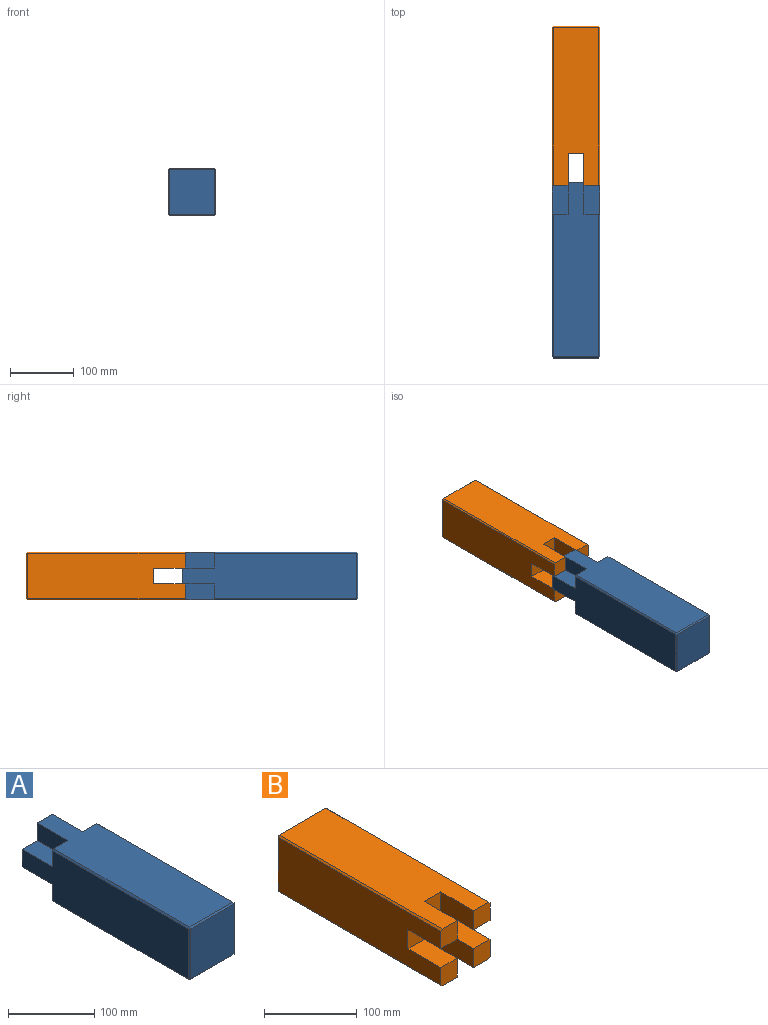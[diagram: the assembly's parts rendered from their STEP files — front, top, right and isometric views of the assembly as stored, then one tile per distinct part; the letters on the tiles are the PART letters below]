
ASSEMBLY  parts=2 mates=1
PART A: 30 faces, bbox 75x275x75 mm
  f0: plane 273x71mm, normal (1,0,0), area 17083mm2, adj f2,f10,f11,f12,f14,f18,f19,f20
  f1: plane 273x71mm, normal (0,0,-1), area 17083mm2, adj f2,f13,f14,f16,f17,f20,f25,f26
  f2: plane 75x75mm, normal (0,1,0), area 3125mm2, adj f0,f1,f3,f4,f6,f7,f9,f10
  f3: plane 273x71mm, normal (0,0,1), area 17083mm2, adj f2,f7,f8,f9,f11,f18,f23,f24
  f4: plane 273x71mm, normal (-1,0,0), area 17083mm2, adj f2,f6,f8,f15,f17,f23,f26,f29
  f5: plane 71x71mm, normal (0,-1,0), area 5041mm2, adj f19,f24,f25,f29
  f6: plane 50x25mm, normal (0,0,1), area 1250mm2, adj f2,f4,f7,f8
  f7: plane 50x25mm, normal (-1,0,0), area 1250mm2, adj f2,f3,f6,f8
  f8: plane 25x25mm, normal (0,1,0), area 623mm2, adj f3,f4,f6,f7,f23
  f9: plane 50x25mm, normal (1,0,0), area 1250mm2, adj f2,f3,f10,f11
  f10: plane 50x25mm, normal (0,0,1), area 1250mm2, adj f0,f2,f9,f11
  f11: plane 25x25mm, normal (0,1,0), area 623mm2, adj f0,f3,f9,f10,f18
  f12: plane 50x25mm, normal (0,0,-1), area 1250mm2, adj f0,f2,f13,f14
  f13: plane 50x25mm, normal (1,0,0), area 1250mm2, adj f1,f2,f12,f14
  f14: plane 25x25mm, normal (0,1,0), area 623mm2, adj f0,f1,f12,f13,f20
  f15: plane 50x25mm, normal (0,0,-1), area 1250mm2, adj f2,f4,f16,f17
  f16: plane 50x25mm, normal (-1,0,0), area 1250mm2, adj f1,f2,f15,f17
  f17: plane 25x25mm, normal (0,1,0), area 623mm2, adj f1,f4,f15,f16,f26
  f18: plane 223x2mm, normal (0.71,0,0.71), area 630.7mm2, adj f0,f3,f11,f21
  f19: plane 71x2mm, normal (0.71,-0.71,0), area 200.8mm2, adj f0,f5,f21,f22
  f20: plane 223x2mm, normal (0.71,0,-0.71), area 630.7mm2, adj f0,f1,f14,f22
  f21: plane 2x2mm, normal (0.58,-0.58,0.58), area 3.5mm2, adj f18,f19,f24
  f22: plane 2x2mm, normal (0.58,-0.58,-0.58), area 3.5mm2, adj f19,f20,f25
  f23: plane 223x2mm, normal (-0.71,0,0.71), area 630.7mm2, adj f3,f4,f8,f27
  f24: plane 71x2mm, normal (0,-0.71,0.71), area 200.8mm2, adj f3,f5,f21,f27
  f25: plane 71x2mm, normal (0,-0.71,-0.71), area 200.8mm2, adj f1,f5,f22,f28
  f26: plane 223x2mm, normal (-0.71,0,-0.71), area 630.7mm2, adj f1,f4,f17,f28
  f27: plane 2x2mm, normal (-0.58,-0.58,0.58), area 3.5mm2, adj f23,f24,f29
  f28: plane 2x2mm, normal (-0.58,-0.58,-0.58), area 3.5mm2, adj f25,f26,f29
  f29: plane 71x2mm, normal (-0.71,-0.71,0), area 200.8mm2, adj f4,f5,f27,f28
PART B: 30 faces, bbox 75x250x75 mm
  f0: plane 75x75mm, normal (0,-1,0), area 3125mm2, adj f1,f2,f3,f4,f6,f7,f9,f10
  f1: plane 248x71mm, normal (1,0,0), area 16358mm2, adj f0,f10,f11,f12,f14,f18,f19,f20
  f2: plane 248x71mm, normal (0,0,1), area 16358mm2, adj f0,f7,f8,f9,f11,f18,f23,f24
  f3: plane 248x71mm, normal (-1,0,0), area 16358mm2, adj f0,f6,f8,f15,f17,f24,f25,f29
  f4: plane 248x71mm, normal (0,0,-1), area 16358mm2, adj f0,f13,f14,f16,f17,f19,f25,f26
  f5: plane 71x71mm, normal (0,1,0), area 5041mm2, adj f20,f23,f26,f29
  f6: plane 50x25mm, normal (0,0,-1), area 1250mm2, adj f0,f3,f7,f8
  f7: plane 50x25mm, normal (1,0,0), area 1250mm2, adj f0,f2,f6,f8
  f8: plane 25x25mm, normal (0,-1,0), area 623mm2, adj f2,f3,f6,f7,f24
  f9: plane 50x25mm, normal (-1,0,0), area 1250mm2, adj f0,f2,f10,f11
  f10: plane 50x25mm, normal (0,0,-1), area 1250mm2, adj f0,f1,f9,f11
  f11: plane 25x25mm, normal (0,-1,0), area 623mm2, adj f1,f2,f9,f10,f18
  f12: plane 50x25mm, normal (0,0,1), area 1250mm2, adj f0,f1,f13,f14
  f13: plane 50x25mm, normal (-1,0,0), area 1250mm2, adj f0,f4,f12,f14
  f14: plane 25x25mm, normal (0,-1,0), area 623mm2, adj f1,f4,f12,f13,f19
  f15: plane 50x25mm, normal (0,0,1), area 1250mm2, adj f0,f3,f16,f17
  f16: plane 50x25mm, normal (1,0,0), area 1250mm2, adj f0,f4,f15,f17
  f17: plane 25x25mm, normal (0,-1,0), area 623mm2, adj f3,f4,f15,f16,f25
  f18: plane 248x2mm, normal (0.71,0,0.71), area 701.4mm2, adj f1,f2,f11,f21
  f19: plane 248x2mm, normal (0.71,0,-0.71), area 701.4mm2, adj f1,f4,f14,f22
  f20: plane 71x2mm, normal (0.71,0.71,0), area 200.8mm2, adj f1,f5,f21,f22
  f21: plane 2x2mm, normal (0.58,0.58,0.58), area 3.5mm2, adj f18,f20,f23
  f22: plane 2x2mm, normal (0.58,0.58,-0.58), area 3.5mm2, adj f19,f20,f26
  f23: plane 71x2mm, normal (0,0.71,0.71), area 200.8mm2, adj f2,f5,f21,f27
  f24: plane 248x2mm, normal (-0.71,0,0.71), area 701.4mm2, adj f2,f3,f8,f27
  f25: plane 248x2mm, normal (-0.71,0,-0.71), area 701.4mm2, adj f3,f4,f17,f28
  f26: plane 71x2mm, normal (0,0.71,-0.71), area 200.8mm2, adj f4,f5,f22,f28
  f27: plane 2x2mm, normal (-0.58,0.58,0.58), area 3.5mm2, adj f23,f24,f29
  f28: plane 2x2mm, normal (-0.58,0.58,-0.58), area 3.5mm2, adj f25,f26,f29
  f29: plane 71x2mm, normal (-0.71,0.71,0), area 200.8mm2, adj f3,f5,f27,f28
PLACE A t=(14.76,-90,33.83)mm
PLACE B t=(14.76,-43.93,33.83)mm fixed
MATE slider A.f2 <-> B.f0  axis (0,1,0) through (14.76,-90,33.83)mm
